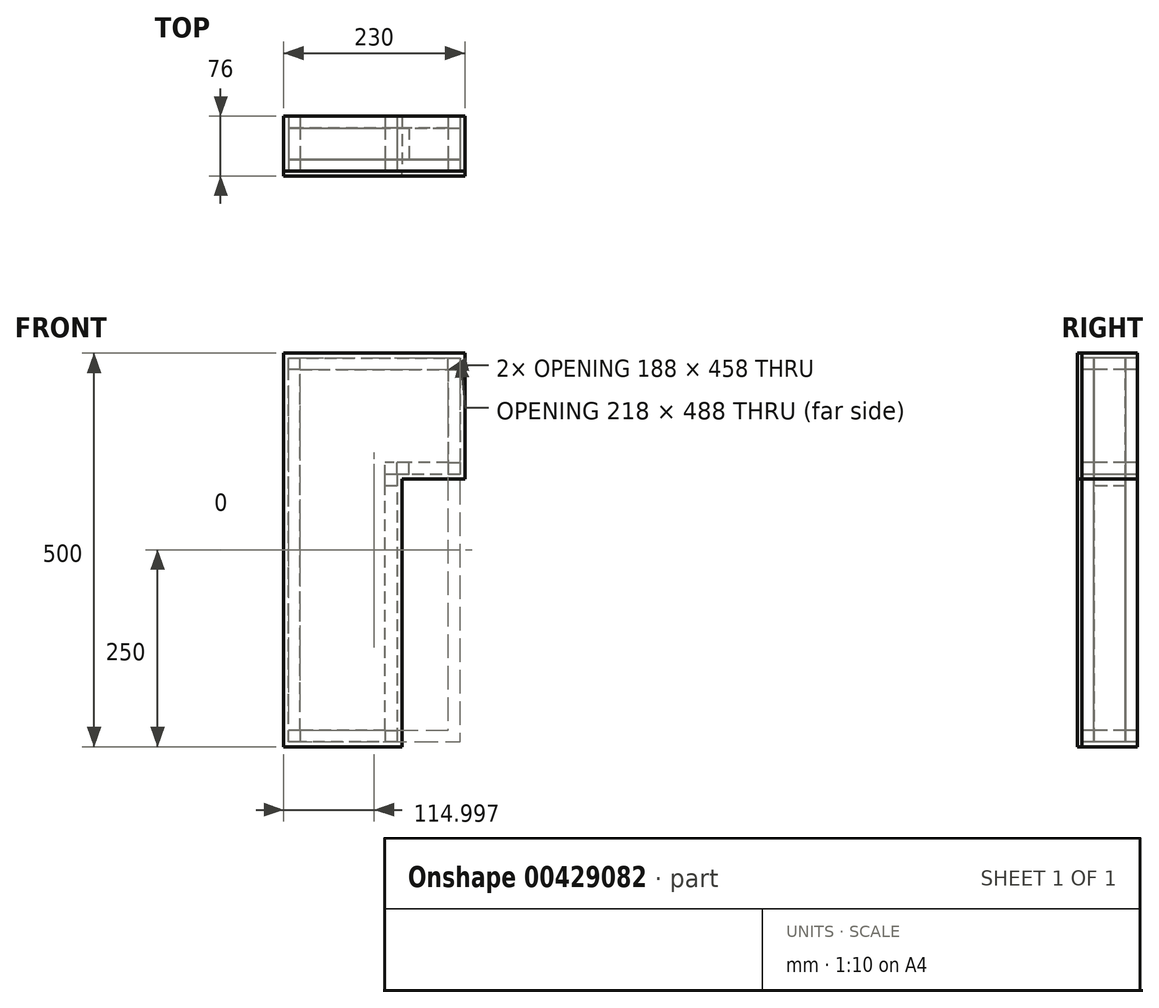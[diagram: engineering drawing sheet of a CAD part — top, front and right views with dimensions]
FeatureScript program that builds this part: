
annotation { "Feature Type Name" : "Feature", "Feature Type Description" : "" }
export const myFeature = defineFeature(function(context is Context, id is Id, definition is map)
    precondition{}
    {
        {
            var Q0;
            Q0=qCreatedBy(makeId("Front.planeOp"),FACE);
            var sketch = newSketch(context, id + "F0", { "sketchPlane" : qUnion([Q0])});
            skLineSegment(sketch, "E0", {"start": v(-41.51, 0) * mm, "end": v(-41.51, 500) * mm});
            skLineSegment(sketch, "E1", {"start": v(-41.51, 500) * mm, "end": v(188.49, 500) * mm});
            skLineSegment(sketch, "E2", {"start": v(188.49, 500) * mm, "end": v(188.49, 340) * mm});
            skLineSegment(sketch, "E3", {"start": v(188.49, 340) * mm, "end": v(108.49, 340) * mm});
            skLineSegment(sketch, "E4", {"start": v(108.49, 340) * mm, "end": v(108.49, 0) * mm});
            skLineSegment(sketch, "E5", {"start": v(108.49, 0) * mm, "end": v(-41.51, 0) * mm});
            skSolve(sketch);
        }
        {
            var Q0;
            Q0=makeQuery(id+"F0.imprint","IMPRINT",FACE,{"disambiguationData":[TD([[makeQuery(id+"F0.imprint","IMPRINT",EDGE,{"derivedFrom":sQuery(id+"F0.wireOp",EDGE,"E0")}),-1.0]])]});
            var Q1;
            Q1=sQuery(id+"F0.wireOp",EDGE,"E1");
            var Q2;
            Q2=sQuery(id+"F0.wireOp",EDGE,"E0");
            var Q3;
            Q3=sQuery(id+"F0.wireOp",EDGE,"E5");
            var Q4;
            Q4=sQuery(id+"F0.wireOp",EDGE,"E4");
            var Q5;
            Q5=sQuery(id+"F0.wireOp",EDGE,"E3");
            var Q6;
            Q6=sQuery(id+"F0.wireOp",EDGE,"E2");
            extrude(context, id + "F1", {"entities" : qUnion([Q0]), "surfaceEntities" : qUnion([Q1, Q2, Q3, Q4, Q5, Q6]), "depth" : 6 * mm});
        }
        {
            var Q0;
            Q0=makeQuery(id+"F1.opExtrude","CAP_FACE",FACE,{"disambiguationData":[OSD([sQuery(id+"F0.wireOp",EDGE,"E0"),sQuery(id+"F0.wireOp",EDGE,"E1"),sQuery(id+"F0.wireOp",EDGE,"E2"),sQuery(id+"F0.wireOp",EDGE,"E3"),sQuery(id+"F0.wireOp",EDGE,"E4"),sQuery(id+"F0.wireOp",EDGE,"E5")])],"isStart":true});
            var sketch = newSketch(context, id + "F2", { "sketchPlane" : qUnion([Q0])});
            skLineSegment(sketch, "E6.bottom", {"start": v(-188.49, 500) * mm, "end": v(-182.49, 500) * mm});
            skLineSegment(sketch, "E6.top", {"start": v(-188.49, 340) * mm, "end": v(-182.49, 340) * mm});
            skLineSegment(sketch, "E6.left", {"start": v(-188.49, 500) * mm, "end": v(-188.49, 340) * mm});
            skLineSegment(sketch, "E6.right", {"start": v(-182.49, 500) * mm, "end": v(-182.49, 340) * mm});
            skLineSegment(sketch, "E7.bottom", {"start": v(-182.49, 340) * mm, "end": v(-108.49, 340) * mm});
            skLineSegment(sketch, "E7.top", {"start": v(-182.49, 346) * mm, "end": v(-108.49, 346) * mm});
            skLineSegment(sketch, "E7.left", {"start": v(-182.49, 340) * mm, "end": v(-182.49, 346) * mm});
            skLineSegment(sketch, "E7.right", {"start": v(-108.49, 340) * mm, "end": v(-108.49, 346) * mm});
            skLineSegment(sketch, "E8.bottom", {"start": v(-102.49, 346) * mm, "end": v(-108.49, 346) * mm});
            skLineSegment(sketch, "E8.top", {"start": v(-102.49, 0) * mm, "end": v(-108.49, 0) * mm});
            skLineSegment(sketch, "E8.left", {"start": v(-102.49, 346) * mm, "end": v(-102.49, 0) * mm});
            skLineSegment(sketch, "E8.right", {"start": v(-108.49, 346) * mm, "end": v(-108.49, 0) * mm});
            skLineSegment(sketch, "E9.bottom", {"start": v(-102.49, 0) * mm, "end": v(41.51, 0) * mm});
            skLineSegment(sketch, "E9.top", {"start": v(-102.49, 6) * mm, "end": v(41.51, 6) * mm});
            skLineSegment(sketch, "E9.left", {"start": v(-102.49, 0) * mm, "end": v(-102.49, 6) * mm});
            skLineSegment(sketch, "E9.right", {"start": v(41.51, 0) * mm, "end": v(41.51, 6) * mm});
            skLineSegment(sketch, "E10.bottom", {"start": v(41.51, 6) * mm, "end": v(35.51, 6) * mm});
            skLineSegment(sketch, "E10.top", {"start": v(41.51, 500) * mm, "end": v(35.51, 500) * mm});
            skLineSegment(sketch, "E10.left", {"start": v(41.51, 6) * mm, "end": v(41.51, 500) * mm});
            skLineSegment(sketch, "E10.right", {"start": v(35.51, 6) * mm, "end": v(35.51, 500) * mm});
            skLineSegment(sketch, "E11.bottom", {"start": v(35.51, 500) * mm, "end": v(-182.49, 500) * mm});
            skLineSegment(sketch, "E11.top", {"start": v(35.51, 494) * mm, "end": v(-182.49, 494) * mm});
            skLineSegment(sketch, "E11.left", {"start": v(35.51, 500) * mm, "end": v(35.51, 494) * mm});
            skLineSegment(sketch, "E11.right", {"start": v(-182.49, 500) * mm, "end": v(-182.49, 494) * mm});
            skSolve(sketch);
        }
        {
            var Q0;
            Q0 = qSketchRegion(id + "F2", true);
            extrude(context, id + "F3", {"entities" : qUnion([Q0]), "depth" : 70 * mm});
        }
        {
            var Q0;
            Q0=makeQuery(id+"F3.opExtrude","CAP_FACE",FACE,{"disambiguationData":[OSD([sQuery(id+"F2.wireOp",EDGE,"E6.bottom"),sQuery(id+"F2.wireOp",EDGE,"E6.top"),sQuery(id+"F2.wireOp",EDGE,"E6.left"),sQuery(id+"F2.wireOp",EDGE,"E6.right"),sQuery(id+"F2.wireOp",EDGE,"E7.bottom"),sQuery(id+"F2.wireOp",EDGE,"E7.top"),sQuery(id+"F2.wireOp",EDGE,"E8.bottom"),sQuery(id+"F2.wireOp",EDGE,"E8.top"),sQuery(id+"F2.wireOp",EDGE,"E8.left"),sQuery(id+"F2.wireOp",EDGE,"E8.right"),sQuery(id+"F2.wireOp",EDGE,"E9.bottom"),sQuery(id+"F2.wireOp",EDGE,"E9.top"),sQuery(id+"F2.wireOp",EDGE,"E9.right"),sQuery(id+"F2.wireOp",EDGE,"E10.top"),sQuery(id+"F2.wireOp",EDGE,"E10.left"),sQuery(id+"F2.wireOp",EDGE,"E10.right"),sQuery(id+"F2.wireOp",EDGE,"E11.bottom"),sQuery(id+"F2.wireOp",EDGE,"E11.top")])],"isStart":true});
            var sketch = newSketch(context, id + "F4", { "sketchPlane" : qUnion([Q0])});
            skLineSegment(sketch, "E12.bottom", {"start": v(-35.51, 494) * mm, "end": v(182.49, 494) * mm});
            skLineSegment(sketch, "E12.top", {"start": v(-35.51, 479) * mm, "end": v(182.49, 479) * mm});
            skLineSegment(sketch, "E12.left", {"start": v(-35.51, 494) * mm, "end": v(-35.51, 479) * mm});
            skLineSegment(sketch, "E12.right", {"start": v(182.49, 494) * mm, "end": v(182.49, 479) * mm});
            skLineSegment(sketch, "E13.bottom", {"start": v(182.49, 479) * mm, "end": v(167.49, 479) * mm});
            skLineSegment(sketch, "E13.top", {"start": v(182.49, 346) * mm, "end": v(167.49, 346) * mm});
            skLineSegment(sketch, "E13.left", {"start": v(182.49, 479) * mm, "end": v(182.49, 346) * mm});
            skLineSegment(sketch, "E13.right", {"start": v(167.49, 479) * mm, "end": v(167.49, 346) * mm});
            skLineSegment(sketch, "E14.bottom", {"start": v(167.49, 346) * mm, "end": v(87.49, 346) * mm});
            skLineSegment(sketch, "E14.top", {"start": v(167.49, 361) * mm, "end": v(87.49, 361) * mm});
            skLineSegment(sketch, "E14.left", {"start": v(167.49, 346) * mm, "end": v(167.49, 361) * mm});
            skLineSegment(sketch, "E14.right", {"start": v(87.49, 346) * mm, "end": v(87.49, 361) * mm});
            skLineSegment(sketch, "E15.bottom", {"start": v(87.49, 346) * mm, "end": v(102.49, 346) * mm});
            skLineSegment(sketch, "E15.top", {"start": v(87.49, 6) * mm, "end": v(102.49, 6) * mm});
            skLineSegment(sketch, "E15.left", {"start": v(87.49, 346) * mm, "end": v(87.49, 6) * mm});
            skLineSegment(sketch, "E15.right", {"start": v(102.49, 346) * mm, "end": v(102.49, 6) * mm});
            skLineSegment(sketch, "E16.bottom", {"start": v(87.49, 6) * mm, "end": v(-35.51, 6) * mm});
            skLineSegment(sketch, "E16.top", {"start": v(87.49, 21) * mm, "end": v(-35.51, 21) * mm});
            skLineSegment(sketch, "E16.left", {"start": v(87.49, 6) * mm, "end": v(87.49, 21) * mm});
            skLineSegment(sketch, "E16.right", {"start": v(-35.51, 6) * mm, "end": v(-35.51, 21) * mm});
            skLineSegment(sketch, "E17.bottom", {"start": v(-35.51, 21) * mm, "end": v(-20.51, 21) * mm});
            skLineSegment(sketch, "E17.top", {"start": v(-35.51, 479) * mm, "end": v(-20.51, 479) * mm});
            skLineSegment(sketch, "E17.left", {"start": v(-35.51, 21) * mm, "end": v(-35.51, 479) * mm});
            skLineSegment(sketch, "E17.right", {"start": v(-20.51, 21) * mm, "end": v(-20.51, 479) * mm});
            skSolve(sketch);
        }
        {
            var Q0;
            Q0 = qSketchRegion(id + "F4", true);
            extrude(context, id + "F5", {"entities" : qUnion([Q0]), "oppositeDirection" : true, "depth" : 15 * mm});
        }
        {
            var Q0;
            Q0=makeQuery(id+"F5.opExtrude","CAP_FACE",FACE,{"disambiguationData":[OSD([sQuery(id+"F4.wireOp",EDGE,"E12.bottom"),sQuery(id+"F4.wireOp",EDGE,"E12.top"),sQuery(id+"F4.wireOp",EDGE,"E12.left"),sQuery(id+"F4.wireOp",EDGE,"E12.right"),sQuery(id+"F4.wireOp",EDGE,"E13.top"),sQuery(id+"F4.wireOp",EDGE,"E13.left"),sQuery(id+"F4.wireOp",EDGE,"E13.right"),sQuery(id+"F4.wireOp",EDGE,"E14.bottom"),sQuery(id+"F4.wireOp",EDGE,"E14.top"),sQuery(id+"F4.wireOp",EDGE,"E14.right"),sQuery(id+"F4.wireOp",EDGE,"E15.top"),sQuery(id+"F4.wireOp",EDGE,"E15.left"),sQuery(id+"F4.wireOp",EDGE,"E15.right"),sQuery(id+"F4.wireOp",EDGE,"E16.bottom"),sQuery(id+"F4.wireOp",EDGE,"E16.top"),sQuery(id+"F4.wireOp",EDGE,"E16.right"),sQuery(id+"F4.wireOp",EDGE,"E17.left"),sQuery(id+"F4.wireOp",EDGE,"E17.right")])],"isStart":false});
            var sketch = newSketch(context, id + "F6", { "sketchPlane" : qUnion([Q0])});
            skLineSegment(sketch, "E18.bottom", {"start": v(-167.49, 479) * mm, "end": v(-182.49, 479) * mm});
            skLineSegment(sketch, "E18.top", {"start": v(-167.49, 494) * mm, "end": v(-182.49, 494) * mm});
            skLineSegment(sketch, "E18.left", {"start": v(-167.49, 479) * mm, "end": v(-167.49, 494) * mm});
            skLineSegment(sketch, "E18.right", {"start": v(-182.49, 479) * mm, "end": v(-182.49, 494) * mm});
            skLineSegment(sketch, "E19.bottom", {"start": v(-167.49, 361) * mm, "end": v(-182.49, 361) * mm});
            skLineSegment(sketch, "E19.top", {"start": v(-167.49, 346) * mm, "end": v(-182.49, 346) * mm});
            skLineSegment(sketch, "E19.left", {"start": v(-167.49, 361) * mm, "end": v(-167.49, 346) * mm});
            skLineSegment(sketch, "E19.right", {"start": v(-182.49, 361) * mm, "end": v(-182.49, 346) * mm});
            skLineSegment(sketch, "E20.bottom", {"start": v(-102.49, 346) * mm, "end": v(-117.49, 346) * mm});
            skLineSegment(sketch, "E20.top", {"start": v(-102.49, 361) * mm, "end": v(-117.49, 361) * mm});
            skLineSegment(sketch, "E20.left", {"start": v(-102.49, 346) * mm, "end": v(-102.49, 361) * mm});
            skLineSegment(sketch, "E20.right", {"start": v(-117.49, 346) * mm, "end": v(-117.49, 361) * mm});
            skLineSegment(sketch, "E21.bottom", {"start": v(-102.49, 346) * mm, "end": v(-87.49, 346) * mm});
            skLineSegment(sketch, "E21.top", {"start": v(-102.49, 331) * mm, "end": v(-87.49, 331) * mm});
            skLineSegment(sketch, "E21.left", {"start": v(-102.49, 346) * mm, "end": v(-102.49, 331) * mm});
            skLineSegment(sketch, "E21.right", {"start": v(-87.49, 346) * mm, "end": v(-87.49, 331) * mm});
            skLineSegment(sketch, "E22.bottom", {"start": v(-87.49, 21) * mm, "end": v(-102.49, 21) * mm});
            skLineSegment(sketch, "E22.top", {"start": v(-87.49, 6) * mm, "end": v(-102.49, 6) * mm});
            skLineSegment(sketch, "E22.left", {"start": v(-87.49, 21) * mm, "end": v(-87.49, 6) * mm});
            skLineSegment(sketch, "E22.right", {"start": v(-102.49, 21) * mm, "end": v(-102.49, 6) * mm});
            skLineSegment(sketch, "E23.bottom", {"start": v(20.51, 21) * mm, "end": v(35.51, 21) * mm});
            skLineSegment(sketch, "E23.top", {"start": v(20.51, 6) * mm, "end": v(35.51, 6) * mm});
            skLineSegment(sketch, "E23.left", {"start": v(20.51, 21) * mm, "end": v(20.51, 6) * mm});
            skLineSegment(sketch, "E23.right", {"start": v(35.51, 21) * mm, "end": v(35.51, 6) * mm});
            skLineSegment(sketch, "E24.bottom", {"start": v(20.51, 479) * mm, "end": v(35.51, 479) * mm});
            skLineSegment(sketch, "E24.top", {"start": v(20.51, 494) * mm, "end": v(35.51, 494) * mm});
            skLineSegment(sketch, "E24.left", {"start": v(20.51, 479) * mm, "end": v(20.51, 494) * mm});
            skLineSegment(sketch, "E24.right", {"start": v(35.51, 479) * mm, "end": v(35.51, 494) * mm});
            skSolve(sketch);
        }
        {
            var Q0;
            Q0 = qSketchRegion(id + "F6", true);
            extrude(context, id + "F7", {"entities" : qUnion([Q0]), "depth" : 40 * mm});
        }
        {
            var Q0;
            Q0=makeQuery(id+"F7.opExtrude","CAP_FACE",FACE,{"disambiguationData":[OSD([sQuery(id+"F6.wireOp",EDGE,"E18.bottom"),sQuery(id+"F6.wireOp",EDGE,"E18.top"),sQuery(id+"F6.wireOp",EDGE,"E18.left"),sQuery(id+"F6.wireOp",EDGE,"E18.right")])],"isStart":false});
            var sketch = newSketch(context, id + "F8", { "sketchPlane" : qUnion([Q0])});
            skLineSegment(sketch, "E25.bottom", {"start": v(-182.49, 494) * mm, "end": v(35.51, 494) * mm});
            skLineSegment(sketch, "E25.top", {"start": v(-182.49, 479) * mm, "end": v(35.51, 479) * mm});
            skLineSegment(sketch, "E25.left", {"start": v(-182.49, 494) * mm, "end": v(-182.49, 479) * mm});
            skLineSegment(sketch, "E25.right", {"start": v(35.51, 494) * mm, "end": v(35.51, 479) * mm});
            skLineSegment(sketch, "E26.bottom", {"start": v(35.51, 479) * mm, "end": v(20.51, 479) * mm});
            skLineSegment(sketch, "E26.top", {"start": v(35.51, 6) * mm, "end": v(20.51, 6) * mm});
            skLineSegment(sketch, "E26.left", {"start": v(35.51, 479) * mm, "end": v(35.51, 6) * mm});
            skLineSegment(sketch, "E26.right", {"start": v(20.51, 479) * mm, "end": v(20.51, 6) * mm});
            skLineSegment(sketch, "E27.bottom", {"start": v(20.51, 6) * mm, "end": v(-102.49, 6) * mm});
            skLineSegment(sketch, "E27.top", {"start": v(20.51, 21) * mm, "end": v(-102.49, 21) * mm});
            skLineSegment(sketch, "E27.left", {"start": v(20.51, 6) * mm, "end": v(20.51, 21) * mm});
            skLineSegment(sketch, "E27.right", {"start": v(-102.49, 6) * mm, "end": v(-102.49, 21) * mm});
            skLineSegment(sketch, "E28.bottom", {"start": v(-102.49, 21) * mm, "end": v(-87.49, 21) * mm});
            skLineSegment(sketch, "E28.top", {"start": v(-102.49, 361) * mm, "end": v(-87.49, 361) * mm});
            skLineSegment(sketch, "E28.left", {"start": v(-102.49, 21) * mm, "end": v(-102.49, 361) * mm});
            skLineSegment(sketch, "E28.right", {"start": v(-87.49, 21) * mm, "end": v(-87.49, 361) * mm});
            skLineSegment(sketch, "E29.bottom", {"start": v(-102.49, 361) * mm, "end": v(-182.49, 361) * mm});
            skLineSegment(sketch, "E29.top", {"start": v(-102.49, 346) * mm, "end": v(-182.49, 346) * mm});
            skLineSegment(sketch, "E29.left", {"start": v(-102.49, 361) * mm, "end": v(-102.49, 346) * mm});
            skLineSegment(sketch, "E29.right", {"start": v(-182.49, 361) * mm, "end": v(-182.49, 346) * mm});
            skLineSegment(sketch, "E30.bottom", {"start": v(-182.49, 361) * mm, "end": v(-167.49, 361) * mm});
            skLineSegment(sketch, "E30.top", {"start": v(-182.49, 479) * mm, "end": v(-167.49, 479) * mm});
            skLineSegment(sketch, "E30.left", {"start": v(-182.49, 361) * mm, "end": v(-182.49, 479) * mm});
            skLineSegment(sketch, "E30.right", {"start": v(-167.49, 361) * mm, "end": v(-167.49, 479) * mm});
            skSolve(sketch);
        }
        {
            var Q0;
            Q0 = qSketchRegion(id + "F8", true);
            extrude(context, id + "F9", {"entities" : qUnion([Q0]), "depth" : 15 * mm});
        }
    });
